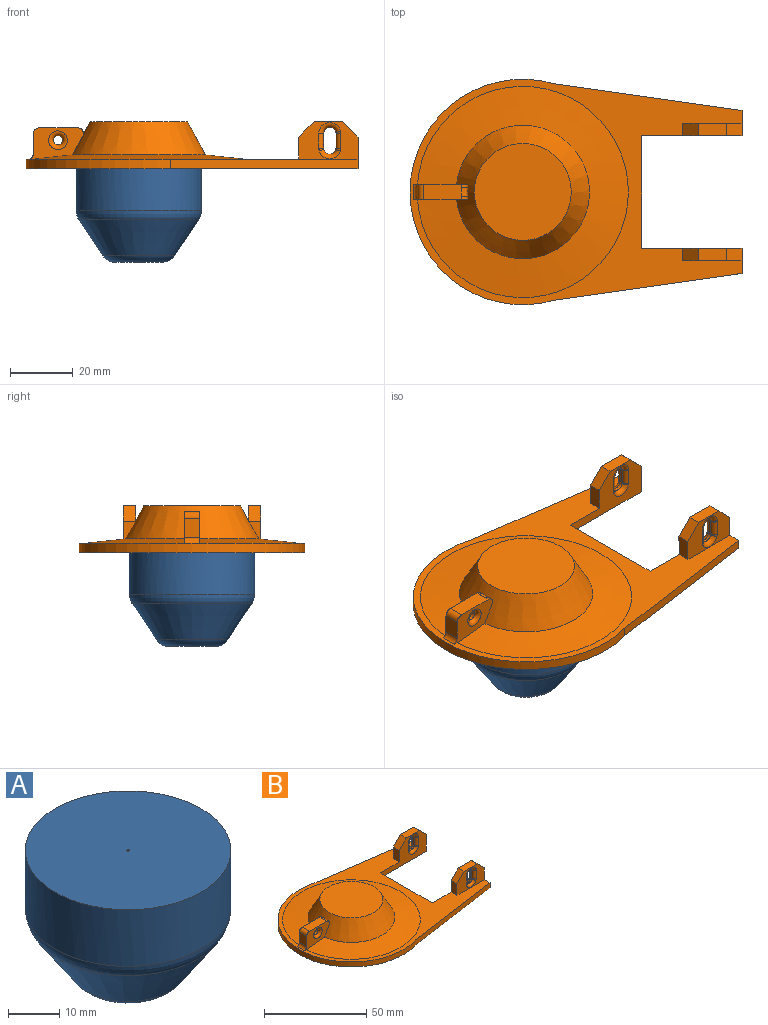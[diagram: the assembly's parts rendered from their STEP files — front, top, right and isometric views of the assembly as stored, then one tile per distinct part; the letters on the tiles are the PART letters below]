
ASSEMBLY  parts=2 mates=1
PART A: 12 faces, bbox 43.3x43.3x30.1 mm
  f0: plane 40x40mm, normal (0,0,1), area 1256.4mm2, adj f2,f8
  f1: cone r=20mm half-angle=33.7deg, axis (0,0,1), area 1336.6mm2, adj f10,f11
  f2: cylinder r=20mm len=40mm, axis (0,0,1), area 1694.7mm2, adj f0,f11
  f3: cylinder r=8mm len=16mm, axis (0,0,-1), area 100.5mm2, adj f5,f10
  f4: plane 36x36mm, normal (0,0,-1), area 1017.9mm2, adj f7
  f5: plane 17.86x17.86mm, normal (0,0,1), area 49.4mm2, adj f3,f6
  f6: cone r=18.34mm half-angle=33.7deg, axis (0,0,1), area 1383.4mm2, adj f5,f7
  f7: cylinder r=18mm len=36mm, axis (0,0,1), area 1401.8mm2, adj f4,f6
  f8: cylinder r=0.25mm len=0.5mm, axis (0,0,1), area 0.8mm2, adj f0,f9
  f9: plane 0.5x0.5mm, normal (0,0,1), area 0.2mm2, adj f8
  f10: torus R=7.29mm, axis (0,0,-1), area 260.8mm2, adj f1,f3
  f11: torus R=15mm, axis (0,0,-1), area 364.2mm2, adj f1,f2
PART B: 88 faces, bbox 106.3x72.3x16.4 mm
  f0: plane 32x15mm, normal (0,-1,0), area 227.9mm2, adj f2,f8,f27,f28,f31,f32,f37,f38
  f1: plane 18.94x12mm, normal (0,1,0), area 131.9mm2, adj f2,f27,f31,f32,f45,f46,f49,f50
  f2: plane 106.05x72.05mm, normal (0,0,1), area 1499.5mm2, adj f0,f1,f7,f10,f12,f14,f16,f25
  f3: cylinder r=0.25mm len=0.5mm, axis (0,0,-1), area 0.4mm2, adj f4,f8,f24
  f4: plane 0.5x0.25mm, normal (0,0,-1), area 0.1mm2, adj f3,f24
  f5: plane 1.15x0.27mm, normal (1,0,0), area 0.1mm2, adj f6,f12,f17
  f6: cone r=15.47mm half-angle=28.7deg, axis (0,0,-1), area 1364.9mm2, adj f5,f7,f9,f11,f12,f14,f18
  f7: cone r=21.3mm half-angle=83.8deg, axis (0,0,-1), area 2095.2mm2, adj f2,f6,f12,f14
  f8: plane 106x72mm, normal (0,0,-1), area 5228.6mm2, adj f0,f3,f10,f24,f25,f26,f27,f28
  f9: plane 30.93x30.93mm, normal (0,0,1), area 751.5mm2, adj f6
  f10: cylinder r=36mm len=72mm, axis (0,0,-1), area 400.6mm2, adj f2,f8,f25,f26
  f11: plane 1.16x0.27mm, normal (1,0,0), area 0.1mm2, adj f6,f14,f19
  f12: plane 17.42x10.27mm, normal (0,1,0), area 106.3mm2, adj f2,f5,f6,f7,f13,f15,f16,f17
  f13: plane 6.2x5.03mm, normal (-1,0,0), area 31.2mm2, adj f12,f14,f16,f20
  f14: plane 17.42x10.27mm, normal (0,-1,0), area 106.3mm2, adj f2,f6,f7,f11,f13,f15,f16,f19
  f15: plane 12.03x5.03mm, normal (0,0,1), area 60.5mm2, adj f12,f14,f17,f18,f19,f20
  f16: bspline ~11.98x2.04mm, area 11.2mm2, adj f2,f12,f13,f14
  f17: cylinder r=2mm len=2mm, axis (0,-1,0), area 3.5mm2, adj f5,f12,f15,f18
  f18: bspline ~4.44x2.22mm, area 8.6mm2, adj f6,f15,f17,f19
  f19: cylinder r=2mm len=2mm, axis (0,-1,0), area 3.5mm2, adj f11,f14,f15,f18
  f20: cylinder r=2mm len=5.03mm, axis (0,1,0), area 15.8mm2, adj f12,f13,f14,f15
  f21: cylinder r=1.5mm len=3mm, axis (0,-1,0), area 19.1mm2, adj f22,f23
  f22: torus R=3mm, axis (0,1,0), area 30.3mm2, adj f12,f21
  f23: torus R=3mm, axis (0,1,0), area 30.3mm2, adj f14,f21
  f24: plane 0.5x0.5mm, normal (-1,0,0), area 0.3mm2, adj f3,f4,f8
  f25: plane 59.92x8.56mm, normal (0.14,-0.99,0), area 181.6mm2, adj f2,f8,f10,f30
  f26: plane 59.92x8.56mm, normal (0.14,0.99,0), area 181.6mm2, adj f2,f8,f10,f27
  f27: plane 10.05x8mm, normal (1,0,0), area 52.2mm2, adj f0,f1,f2,f8,f26,f57
  f28: plane 36x3mm, normal (1,0,0), area 108mm2, adj f0,f2,f8,f29
  f29: plane 32x15mm, normal (0,1,0), area 227.9mm2, adj f2,f8,f28,f30,f60,f61,f66,f67
  f30: plane 10.05x8mm, normal (1,0,0), area 52.2mm2, adj f2,f8,f25,f29,f59,f86
  f31: plane 9.06x4mm, normal (0,0,1), area 36.2mm2, adj f0,f1,f57,f58
  f32: plane 7x4mm, normal (-1,0,-0.01), area 28mm2, adj f0,f1,f2,f58
  f33: plane 4.74x1mm, normal (1,0,0), area 4.7mm2, adj f42,f51,f52,f56
  f34: cylinder r=2mm len=3.97mm, axis (0,-1,0), area 5.9mm2, adj f43,f44,f52,f53
  f35: cylinder r=2mm len=3.85mm, axis (0,-1,0), area 5.2mm2, adj f40,f41,f50,f51
  f36: plane 4.83x1mm, normal (-1,0,0), area 4.8mm2, adj f37,f40,f44,f45
  f37: cylinder r=1.5mm len=4.83mm, axis (0,0,-1), area 11.4mm2, adj f0,f36,f38,f39
  f38: torus R=3mm, axis (0,-1,0), area 1.4mm2, adj f0,f37,f40,f41
  f39: torus R=3mm, axis (0,-1,0), area 0.9mm2, adj f0,f37,f43,f44
  f40: cylinder r=1.5mm len=1mm, axis (0,-1,0), area 0.4mm2, adj f35,f36,f38,f46
  f41: torus R=3.5mm, axis (0,-1,0), area 15.5mm2, adj f0,f35,f38,f47
  f42: cylinder r=1.5mm len=4.75mm, axis (0,0,1), area 11.2mm2, adj f0,f33,f47,f48
  f43: torus R=3.5mm, axis (0,-1,0), area 17.7mm2, adj f0,f34,f39,f48
  f44: cylinder r=1.5mm len=1mm, axis (0,-1,0), area 0.3mm2, adj f34,f36,f39,f49
  f45: cylinder r=1.5mm len=4.83mm, axis (0,0,-1), area 11.4mm2, adj f1,f36,f46,f49
  f46: torus R=3mm, axis (0,-1,0), area 1.4mm2, adj f1,f40,f45,f50
  f47: torus R=3mm, axis (0,-1,0), area 1.3mm2, adj f0,f41,f42,f51
  f48: torus R=3mm, axis (0,-1,0), area 0.1mm2, adj f0,f42,f43,f52
  f49: torus R=3mm, axis (0,-1,0), area 0.9mm2, adj f1,f44,f45,f53
  f50: torus R=3.5mm, axis (0,-1,0), area 15.5mm2, adj f1,f35,f46,f54
  f51: cylinder r=1.5mm len=1mm, axis (0,-1,0), area 0.4mm2, adj f33,f35,f47,f54
  f52: cylinder r=1.5mm len=1mm, axis (0,-1,0), area 0mm2, adj f33,f34,f48,f55
  f53: torus R=3.5mm, axis (0,-1,0), area 17.7mm2, adj f1,f34,f49,f55
  f54: torus R=3mm, axis (0,-1,0), area 1.3mm2, adj f1,f50,f51,f56
  f55: torus R=3mm, axis (0,-1,0), area 0.1mm2, adj f1,f52,f53,f56
  f56: cylinder r=1.5mm len=4.75mm, axis (0,0,1), area 11.2mm2, adj f1,f33,f54,f55
  f57: plane 4.95x4.95mm, normal (0.71,0,0.71), area 28mm2, adj f0,f1,f27,f31
  f58: plane 5x4.94mm, normal (-0.71,0,0.7), area 28.1mm2, adj f0,f1,f31,f32
  f59: plane 18.94x12mm, normal (0,-1,0), area 131.9mm2, adj f2,f30,f60,f61,f74,f75,f78,f79
  f60: plane 9.06x4mm, normal (0,0,1), area 36.2mm2, adj f29,f59,f86,f87
  f61: plane 7x4mm, normal (-1,0,-0.01), area 28mm2, adj f2,f29,f59,f87
  f62: plane 4.74x1mm, normal (1,0,0), area 4.7mm2, adj f71,f80,f81,f85
  f63: cylinder r=2mm len=3.97mm, axis (0,1,0), area 5.9mm2, adj f72,f73,f81,f82
  f64: cylinder r=2mm len=3.85mm, axis (0,1,0), area 5.2mm2, adj f69,f70,f79,f80
  f65: plane 4.83x1mm, normal (-1,0,0), area 4.8mm2, adj f66,f69,f73,f74
  f66: cylinder r=1.5mm len=4.83mm, axis (0,0,-1), area 11.4mm2, adj f29,f65,f67,f68
  f67: torus R=3mm, axis (0,1,0), area 1.4mm2, adj f29,f66,f69,f70
  f68: torus R=3mm, axis (0,1,0), area 0.9mm2, adj f29,f66,f72,f73
  f69: cylinder r=1.5mm len=1mm, axis (0,1,0), area 0.4mm2, adj f64,f65,f67,f75
  f70: torus R=3.5mm, axis (0,1,0), area 15.5mm2, adj f29,f64,f67,f76
  f71: cylinder r=1.5mm len=4.75mm, axis (0,0,1), area 11.2mm2, adj f29,f62,f76,f77
  f72: torus R=3.5mm, axis (0,1,0), area 17.7mm2, adj f29,f63,f68,f77
  f73: cylinder r=1.5mm len=1mm, axis (0,1,0), area 0.3mm2, adj f63,f65,f68,f78
  f74: cylinder r=1.5mm len=4.83mm, axis (0,0,-1), area 11.4mm2, adj f59,f65,f75,f78
  f75: torus R=3mm, axis (0,1,0), area 1.4mm2, adj f59,f69,f74,f79
  f76: torus R=3mm, axis (0,1,0), area 1.3mm2, adj f29,f70,f71,f80
  f77: torus R=3mm, axis (0,1,0), area 0.1mm2, adj f29,f71,f72,f81
  f78: torus R=3mm, axis (0,1,0), area 0.9mm2, adj f59,f73,f74,f82
  f79: torus R=3.5mm, axis (0,1,0), area 15.5mm2, adj f59,f64,f75,f83
  f80: cylinder r=1.5mm len=1mm, axis (0,1,0), area 0.4mm2, adj f62,f64,f76,f83
  f81: cylinder r=1.5mm len=1mm, axis (0,1,0), area 0mm2, adj f62,f63,f77,f84
  f82: torus R=3.5mm, axis (0,1,0), area 17.7mm2, adj f59,f63,f78,f84
  f83: torus R=3mm, axis (0,1,0), area 1.3mm2, adj f59,f79,f80,f85
  f84: torus R=3mm, axis (0,1,0), area 0.1mm2, adj f59,f81,f82,f85
  f85: cylinder r=1.5mm len=4.75mm, axis (0,0,1), area 11.2mm2, adj f59,f62,f83,f84
  f86: plane 4.95x4.95mm, normal (0.71,0,0.71), area 28mm2, adj f29,f30,f59,f60
  f87: plane 5x4.94mm, normal (-0.71,0,0.7), area 28.1mm2, adj f29,f59,f60,f61
PLACE A t=(32.17,3.04,-9.6)mm
PLACE B t=(32.17,3.04,-17.74)mm
MATE planar B.f6 <-> A.f1  axis (0,0,-1) through (32.17,3.04,-9.6)mm
